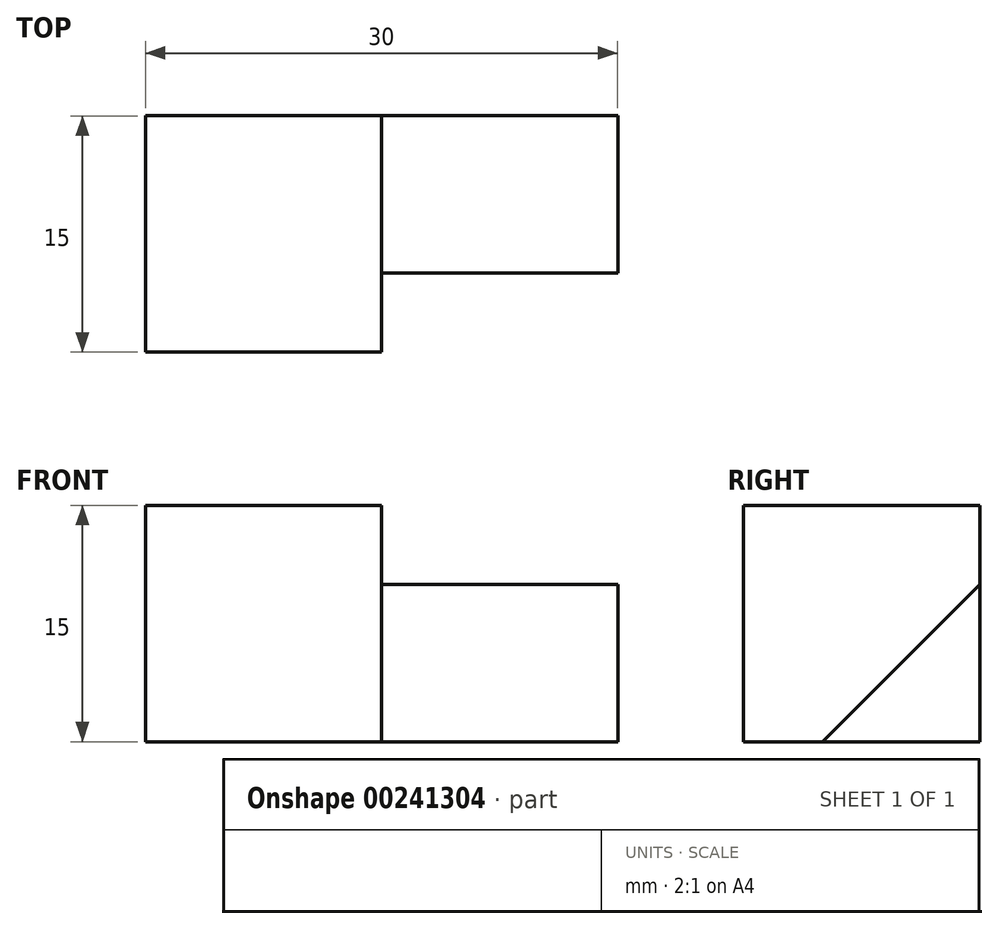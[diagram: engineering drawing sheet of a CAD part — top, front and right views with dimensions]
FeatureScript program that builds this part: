
annotation { "Feature Type Name" : "Feature", "Feature Type Description" : "" }
export const myFeature = defineFeature(function(context is Context, id is Id, definition is map)
    precondition{}
    {
        {
            var Q0;
            Q0=qCreatedBy(makeId("Top.planeOp"),FACE);
            var sketch = newSketch(context, id + "F0", { "sketchPlane" : qUnion([Q0])});
            skLineSegment(sketch, "E0.bottom", {"start": v(-52.68, -24.1) * mm, "end": v(-37.68, -24.1) * mm});
            skLineSegment(sketch, "E0.top", {"start": v(-52.68, -39.1) * mm, "end": v(-37.68, -39.1) * mm});
            skLineSegment(sketch, "E0.left", {"start": v(-52.68, -24.1) * mm, "end": v(-52.68, -39.1) * mm});
            skLineSegment(sketch, "E0.right", {"start": v(-37.68, -24.1) * mm, "end": v(-37.68, -39.1) * mm});
            skSolve(sketch);
        }
        {
            var Q0;
            Q0 = qSketchRegion(id + "F0", true);
            extrude(context, id + "F1", {"entities" : qUnion([Q0]), "depth" : 15 * mm});
        }
        {
            var Q0;
            Q0=makeQuery(id+"F1.opExtrude","SWEPT_FACE",FACE,{"disambiguationData":[OSD([sQuery(id+"F0.wireOp",EDGE,"E0.right")])]});
            var sketch = newSketch(context, id + "F2", { "sketchPlane" : qUnion([Q0])});
            skLineSegment(sketch, "E1", {"start": v(-24.1, 10) * mm, "end": v(-34.1, 0) * mm});
            skSolve(sketch);
        }
        {
            var Q0;
            {var subQ0=sQuery(id+"F2.wireOp",EDGE,"E1");Q0=makeQuery(id+"F2.imprint","IMPRINT",FACE,{"disambiguationData":[TD([[makeQuery(id+"F2.imprint","IMPRINT",EDGE,{"derivedFrom":subQ0}),1.0]])]});}
            extrude(context, id + "F3", {"entities" : qUnion([Q0]), "operationType" : NewBodyOperationType.ADD, "depth" : 15 * mm});
        }
    });
